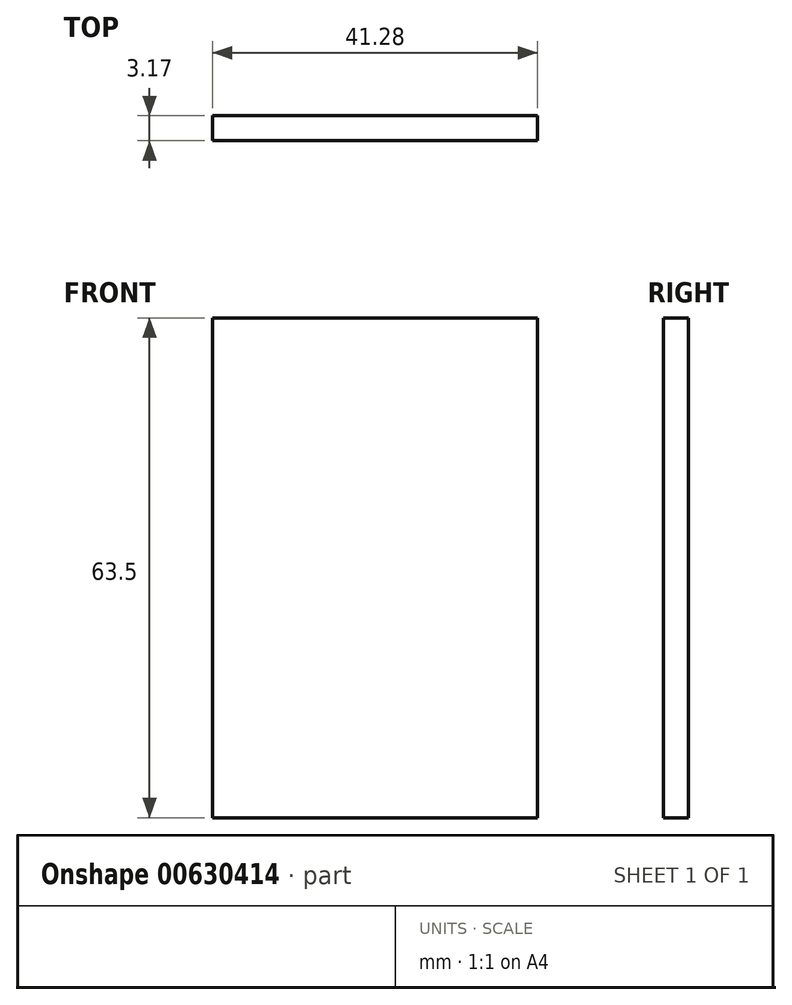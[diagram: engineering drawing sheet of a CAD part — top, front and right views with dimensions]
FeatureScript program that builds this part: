
annotation { "Feature Type Name" : "Feature", "Feature Type Description" : "" }
export const myFeature = defineFeature(function(context is Context, id is Id, definition is map)
    precondition{}
    {
        {
            var Q0;
            Q0=qCreatedBy(makeId("Front.planeOp"),FACE);
            var sketch = newSketch(context, id + "F0", { "sketchPlane" : qUnion([Q0])});
            skLineSegment(sketch, "E0.bottom", {"start": v(20.64, 31.75) * mm, "end": v(-20.64, 31.75) * mm});
            skLineSegment(sketch, "E0.top", {"start": v(20.64, -31.75) * mm, "end": v(-20.64, -31.75) * mm});
            skLineSegment(sketch, "E0.left", {"start": v(20.64, 31.75) * mm, "end": v(20.64, -31.75) * mm});
            skLineSegment(sketch, "E0.right", {"start": v(-20.64, 31.75) * mm, "end": v(-20.64, -31.75) * mm});
            skPoint(sketch, "E0.middle", {"position": v(0, 0) * mm});
            skSolve(sketch);
        }
        {
            var Q0;
            Q0=makeQuery(id+"F0.imprint","IMPRINT",FACE,{"disambiguationData":[TD([[makeQuery(id+"F0.imprint","IMPRINT",EDGE,{"derivedFrom":sQuery(id+"F0.wireOp",EDGE,"E0.bottom")}),1.0]])]});
            extrude(context, id + "F1", {"entities" : qUnion([Q0]), "depth" : 3.17 * mm, "offsetDistance" : 25.4 * mm});
        }
    });
